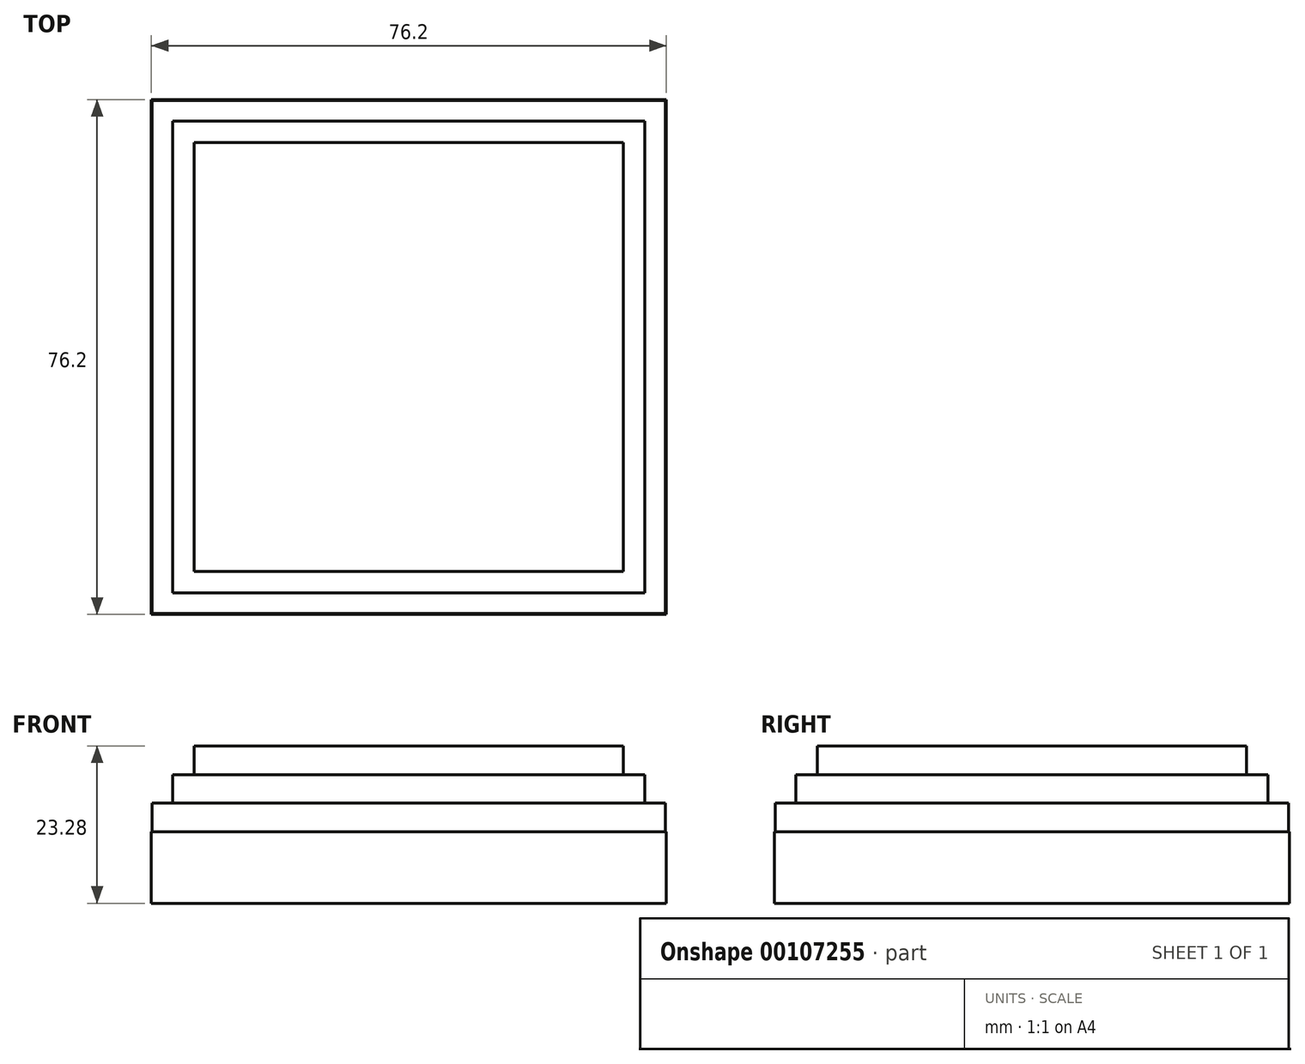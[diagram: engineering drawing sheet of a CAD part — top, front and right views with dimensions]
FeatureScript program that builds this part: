
annotation { "Feature Type Name" : "Feature", "Feature Type Description" : "" }
export const myFeature = defineFeature(function(context is Context, id is Id, definition is map)
    precondition{}
    {
        {
            var Q0;
            Q0=qCreatedBy(makeId("Top.planeOp"),FACE);
            var sketch = newSketch(context, id + "F0", { "sketchPlane" : qUnion([Q0])});
            skLineSegment(sketch, "E0.bottom", {"start": v(38.1, -38.1) * mm, "end": v(-38.1, -38.1) * mm});
            skLineSegment(sketch, "E0.top", {"start": v(38.1, 38.1) * mm, "end": v(-38.1, 38.1) * mm});
            skLineSegment(sketch, "E0.left", {"start": v(38.1, -38.1) * mm, "end": v(38.1, 38.1) * mm});
            skLineSegment(sketch, "E0.right", {"start": v(-38.1, -38.1) * mm, "end": v(-38.1, 38.1) * mm});
            skPoint(sketch, "E0.middle", {"position": v(0, 0) * mm});
            skLineSegment(sketch, "E1.0", {"start": v(28.58, 28.58) * mm, "end": v(-28.57, 28.57) * mm});
            skLineSegment(sketch, "E1.1", {"start": v(28.58, -28.57) * mm, "end": v(28.58, 28.58) * mm});
            skLineSegment(sketch, "E1.2", {"start": v(28.58, -28.57) * mm, "end": v(-28.58, -28.58) * mm});
            skLineSegment(sketch, "E1.3", {"start": v(-28.58, -28.58) * mm, "end": v(-28.57, 28.57) * mm});
            skLineSegment(sketch, "E2.0", {"start": v(25.4, 25.4) * mm, "end": v(-25.4, 25.4) * mm});
            skLineSegment(sketch, "E2.1", {"start": v(25.4, -25.4) * mm, "end": v(25.4, 25.4) * mm});
            skLineSegment(sketch, "E2.2", {"start": v(25.4, -25.4) * mm, "end": v(-25.4, -25.4) * mm});
            skLineSegment(sketch, "E2.3", {"start": v(-25.4, -25.4) * mm, "end": v(-25.4, 25.4) * mm});
            skLineSegment(sketch, "E3.0", {"start": v(31.75, 31.75) * mm, "end": v(-31.75, 31.75) * mm});
            skLineSegment(sketch, "E3.1", {"start": v(31.75, -31.75) * mm, "end": v(31.75, 31.75) * mm});
            skLineSegment(sketch, "E3.2", {"start": v(31.75, -31.75) * mm, "end": v(-31.75, -31.75) * mm});
            skLineSegment(sketch, "E3.3", {"start": v(-31.75, -31.75) * mm, "end": v(-31.75, 31.75) * mm});
            skLineSegment(sketch, "E4.0", {"start": v(34.93, 34.93) * mm, "end": v(-34.93, 34.92) * mm});
            skLineSegment(sketch, "E4.1", {"start": v(34.93, -34.92) * mm, "end": v(34.93, 34.93) * mm});
            skLineSegment(sketch, "E4.2", {"start": v(34.93, -34.92) * mm, "end": v(-34.93, -34.93) * mm});
            skLineSegment(sketch, "E4.3", {"start": v(-34.93, -34.93) * mm, "end": v(-34.93, 34.92) * mm});
            skLineSegment(sketch, "E5.0", {"start": v(37.97, 37.97) * mm, "end": v(-37.97, 37.97) * mm});
            skLineSegment(sketch, "E5.1", {"start": v(37.97, -37.97) * mm, "end": v(37.97, 37.97) * mm});
            skLineSegment(sketch, "E5.2", {"start": v(37.97, -37.97) * mm, "end": v(-37.97, -37.97) * mm});
            skLineSegment(sketch, "E5.3", {"start": v(-37.97, -37.97) * mm, "end": v(-37.97, 37.97) * mm});
            skLineSegment(sketch, "E6", {"start": v(-38.1, 0) * mm, "end": v(38.1, 0) * mm, "construction": true});
            skCircle(sketch, "E7", {"center": v(-34.93, 44.45) * mm, "radius": 6.35 * mm, "construction": true});
            skCircle(sketch, "E8", {"center": v(-25.4, 44.32) * mm, "radius": 6.35 * mm, "construction": true});
            skCircle(sketch, "E9", {"center": v(-15.88, 41.28) * mm, "radius": 6.35 * mm, "construction": true});
            skCircle(sketch, "E10", {"center": v(-6.35, 38.1) * mm, "radius": 6.35 * mm, "construction": true});
            skCircle(sketch, "E11", {"center": v(3.17, 34.93) * mm, "radius": 6.35 * mm, "construction": true});
            skCircle(sketch, "E12", {"center": v(12.7, 31.75) * mm, "radius": 6.35 * mm, "construction": true});
            skSolve(sketch);
        }
        {
            var Q0;
            Q0=makeQuery(id+"F0.imprint","IMPRINT",FACE,{"disambiguationData":[TD([[makeQuery(id+"F0.imprint","IMPRINT",EDGE,{"derivedFrom":sQuery(id+"F0.wireOp",EDGE,"E1.0")}),-1.0]])]});
            var Q1;
            Q1=makeQuery(id+"F0.imprint","IMPRINT",FACE,{"disambiguationData":[TD([[makeQuery(id+"F0.imprint","IMPRINT",EDGE,{"derivedFrom":sQuery(id+"F0.wireOp",EDGE,"E1.0")}),1.0]])]});
            var Q2;
            Q2=makeQuery(id+"F0.imprint","IMPRINT",FACE,{"disambiguationData":[TD([[makeQuery(id+"F0.imprint","IMPRINT",EDGE,{"derivedFrom":sQuery(id+"F0.wireOp",EDGE,"E2.0")}),1.0]])]});
            extrude(context, id + "F1", {"entities" : qUnion([Q0, Q1, Q2]), "depth" : (.5 / 3) * 101.6 * mm});
        }
        {
            var Q0;
            Q0=makeQuery(id+"F0.imprint","IMPRINT",FACE,{"disambiguationData":[TD([[makeQuery(id+"F0.imprint","IMPRINT",EDGE,{"derivedFrom":sQuery(id+"F0.wireOp",EDGE,"E3.0")}),-1.0]])]});
            extrude(context, id + "F2", {"entities" : qUnion([Q0]), "operationType" : NewBodyOperationType.ADD, "depth" : (.5 / 3) * 76.2 * mm});
        }
        {
            var Q0;
            Q0=makeQuery(id+"F0.imprint","IMPRINT",FACE,{"disambiguationData":[TD([[makeQuery(id+"F0.imprint","IMPRINT",EDGE,{"derivedFrom":sQuery(id+"F0.wireOp",EDGE,"E4.0")}),-1.0]])]});
            extrude(context, id + "F3", {"entities" : qUnion([Q0]), "operationType" : NewBodyOperationType.ADD, "depth" : (.5 / 3) * 50.8 * mm});
        }
        {
            var Q0;
            Q0=makeQuery(id+"F0.imprint","IMPRINT",FACE,{"disambiguationData":[TD([[makeQuery(id+"F0.imprint","IMPRINT",EDGE,{"derivedFrom":sQuery(id+"F0.wireOp",EDGE,"E0.bottom")}),-1.0]])]});
            extrude(context, id + "F4", {"entities" : qUnion([Q0]), "operationType" : NewBodyOperationType.ADD, "depth" : 4.23 * mm});
        }
        {
            var Q0;
            {var subQ0=sQuery(id+"F0.wireOp",EDGE,"E5.3");var subQ1=sQuery(id+"F0.wireOp",EDGE,"E5.2");var subQ2=sQuery(id+"F0.wireOp",EDGE,"E5.1");var subQ3=sQuery(id+"F0.wireOp",EDGE,"E5.0");var subQ4=sQuery(id+"F0.wireOp",EDGE,"E4.3");var subQ5=sQuery(id+"F0.wireOp",EDGE,"E4.2");var subQ6=sQuery(id+"F0.wireOp",EDGE,"E4.1");var subQ7=sQuery(id+"F0.wireOp",EDGE,"E4.0");var subQ8=sQuery(id+"F0.wireOp",EDGE,"E3.3");var subQ9=sQuery(id+"F0.wireOp",EDGE,"E3.2");var subQ10=sQuery(id+"F0.wireOp",EDGE,"E3.1");var subQ11=sQuery(id+"F0.wireOp",EDGE,"E3.0");var subQ12=sQuery(id+"F0.wireOp",EDGE,"E1.3");var subQ13=sQuery(id+"F0.wireOp",EDGE,"E1.2");var subQ14=sQuery(id+"F0.wireOp",EDGE,"E1.1");var subQ15=sQuery(id+"F0.wireOp",EDGE,"E1.0");var subQ16=sQuery(id+"F0.wireOp",EDGE,"E2.3");var subQ17=sQuery(id+"F0.wireOp",EDGE,"E2.2");var subQ18=sQuery(id+"F0.wireOp",EDGE,"E2.1");var subQ19=sQuery(id+"F0.wireOp",EDGE,"E2.0");Q0=makeQuery(id+"F4.boolean.opBoolean","MERGE",FACE,{"derivedFrom":[makeQuery(id+"F3.boolean.opBoolean","MERGE",FACE,{"derivedFrom":[makeQuery(id+"F2.boolean.opBoolean","MERGE",FACE,{"derivedFrom":[makeQuery(id+"F1.boolean.opBoolean","MERGE",FACE,{"derivedFrom":[makeQuery(id+"FbizIlvE5IRHbYC_1.boolean.opBoolean","MERGE",FACE,{"derivedFrom":[makeQuery(id+"FWMRa3YnzXB4hih_0.opExtrude","CAP_FACE",FACE,{"disambiguationData":[OSD([subQ19,subQ18,subQ17,subQ16])],"isStart":true}),makeQuery(id+"FbizIlvE5IRHbYC_1.opExtrude","CAP_FACE",FACE,{"disambiguationData":[OSD([subQ15,subQ14,subQ13,subQ12,subQ19,subQ18,subQ17,subQ16])],"isStart":true})]}),makeQuery(id+"F1.opExtrude","CAP_FACE",FACE,{"disambiguationData":[OSD([subQ15,subQ14,subQ13,subQ12,subQ11,subQ10,subQ9,subQ8])],"isStart":true})]}),makeQuery(id+"F2.opExtrude","CAP_FACE",FACE,{"disambiguationData":[OSD([subQ11,subQ10,subQ9,subQ8,subQ7,subQ6,subQ5,subQ4])],"isStart":true})]}),makeQuery(id+"F3.opExtrude","CAP_FACE",FACE,{"disambiguationData":[OSD([subQ7,subQ6,subQ5,subQ4,subQ3,subQ2,subQ1,subQ0])],"isStart":true})]}),makeQuery(id+"F4.opExtrude","CAP_FACE",FACE,{"disambiguationData":[OSD([sQuery(id+"F0.wireOp",EDGE,"E0.bottom"),sQuery(id+"F0.wireOp",EDGE,"E0.top"),sQuery(id+"F0.wireOp",EDGE,"E0.left"),sQuery(id+"F0.wireOp",EDGE,"E0.right"),subQ3,subQ2,subQ1,subQ0])],"isStart":true})]});}
            extrude(context, id + "F5", {"entities" : qUnion([Q0]), "operationType" : NewBodyOperationType.ADD, "depth" : 6.35 * mm});
        }
    });
